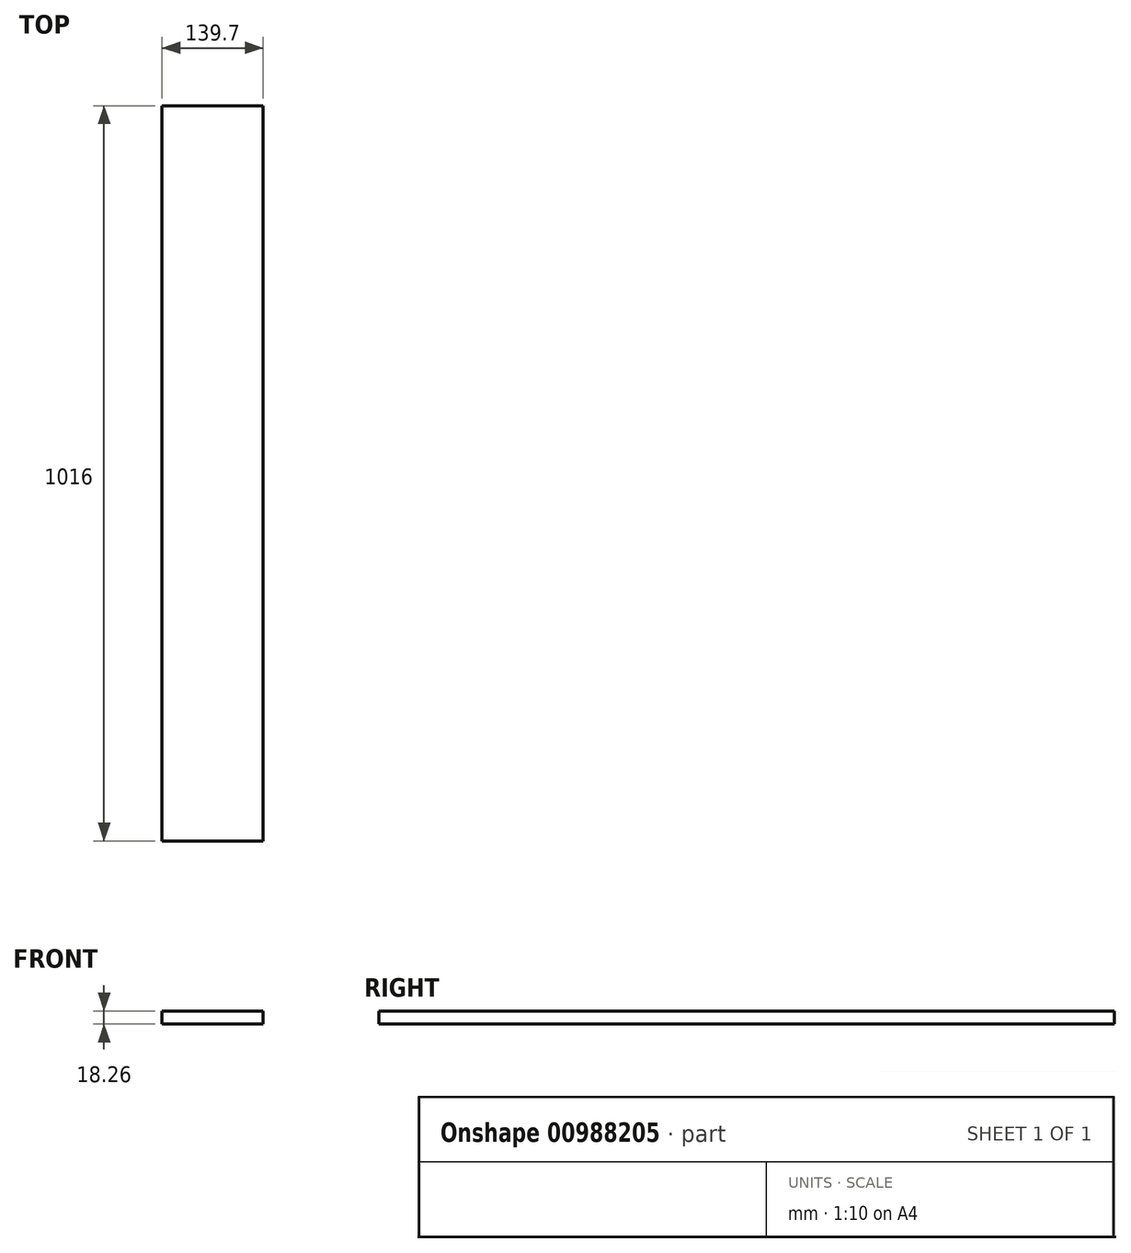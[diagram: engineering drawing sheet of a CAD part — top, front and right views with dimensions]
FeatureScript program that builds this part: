
annotation { "Feature Type Name" : "Feature", "Feature Type Description" : "" }
export const myFeature = defineFeature(function(context is Context, id is Id, definition is map)
    precondition{}
    {
        {
            var Q0;
            Q0=qCreatedBy(makeId("Top.planeOp"),FACE);
            var sketch = newSketch(context, id + "F0", { "sketchPlane" : qUnion([Q0])});
            skLineSegment(sketch, "E0.bottom", {"start": v(69.85, 508) * mm, "end": v(-69.85, 508) * mm});
            skLineSegment(sketch, "E0.top", {"start": v(69.85, -508) * mm, "end": v(-69.85, -508) * mm});
            skLineSegment(sketch, "E0.left", {"start": v(69.85, 508) * mm, "end": v(69.85, -508) * mm});
            skLineSegment(sketch, "E0.right", {"start": v(-69.85, 508) * mm, "end": v(-69.85, -508) * mm});
            skPoint(sketch, "E0.middle", {"position": v(0, 0) * mm});
            skSolve(sketch);
        }
        {
            var Q0;
            Q0=makeQuery(id+"F0.imprint","IMPRINT",FACE,{"disambiguationData":[TD([[makeQuery(id+"F0.imprint","IMPRINT",EDGE,{"derivedFrom":sQuery(id+"F0.wireOp",EDGE,"E0.bottom")}),1.0]])]});
            extrude(context, id + "F1", {"entities" : qUnion([Q0]), "depth" : 18.26 * mm, "offsetDistance" : 25.4 * mm});
        }
    });
